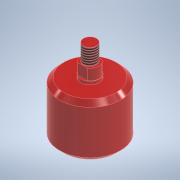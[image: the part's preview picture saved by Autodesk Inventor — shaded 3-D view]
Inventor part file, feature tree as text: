
AUTODESK INVENTOR PART (.ipt)
format: ipt  version: 2022 (Build 260153000, 153)  size: 159,744 bytes
history: native  units: in
note: dims shown in document units (in); Inventor stores cm internally (conversion verified against a paired STEP export)
features: sketch x3, extrude x2, revolve x1, chamfer x1, thread x1, projected_geometry x1
ambient origin geometry x8: Origin, YZ Plane, XZ Plane, XY Plane, X Axis, Y Axis, Z Axis, Center Point
bodies: Solid1 (feature_tree)
feature tree (9):
  revolve  "Revolution1"  [1 undecoded]
  chamfer  "Chamfer1"  Distance=0.2362in
  thread  "Thread1"  [1 undecoded]
  extrude  "Extrusion1"  Depth=1.4961in
  extrude  "Extrusion3"  TaperAngle=90.0deg  [1 undecoded]
  sketch  "Sketch1"  dims[d0=1.1024in d1=0.9449in]
  sketch  "Sketch2"  dims[d2=0.1969in]
  projected_geometry  "Projected Loop1"
  sketch  "Sketch4"  dims[d3=0.315in d4=0.2362in d5=0.3346in d6=1.4961in d7=90.0deg d8=0.0787in d9=0.0787in d10=45.0deg d11=0.2976in d12=0.0in d13=0.265in d14=0.1969in d15=0.0in d20=0.1181in d21=0.748in d22=0.6299in d23=45.0deg d24=0.1969in d25=0.0in]
note: 3 required parameter values undecoded (feature->parameter linkage not recoverable at this tier; creation-order binding heuristic only, values carry confidence <= 0.55)